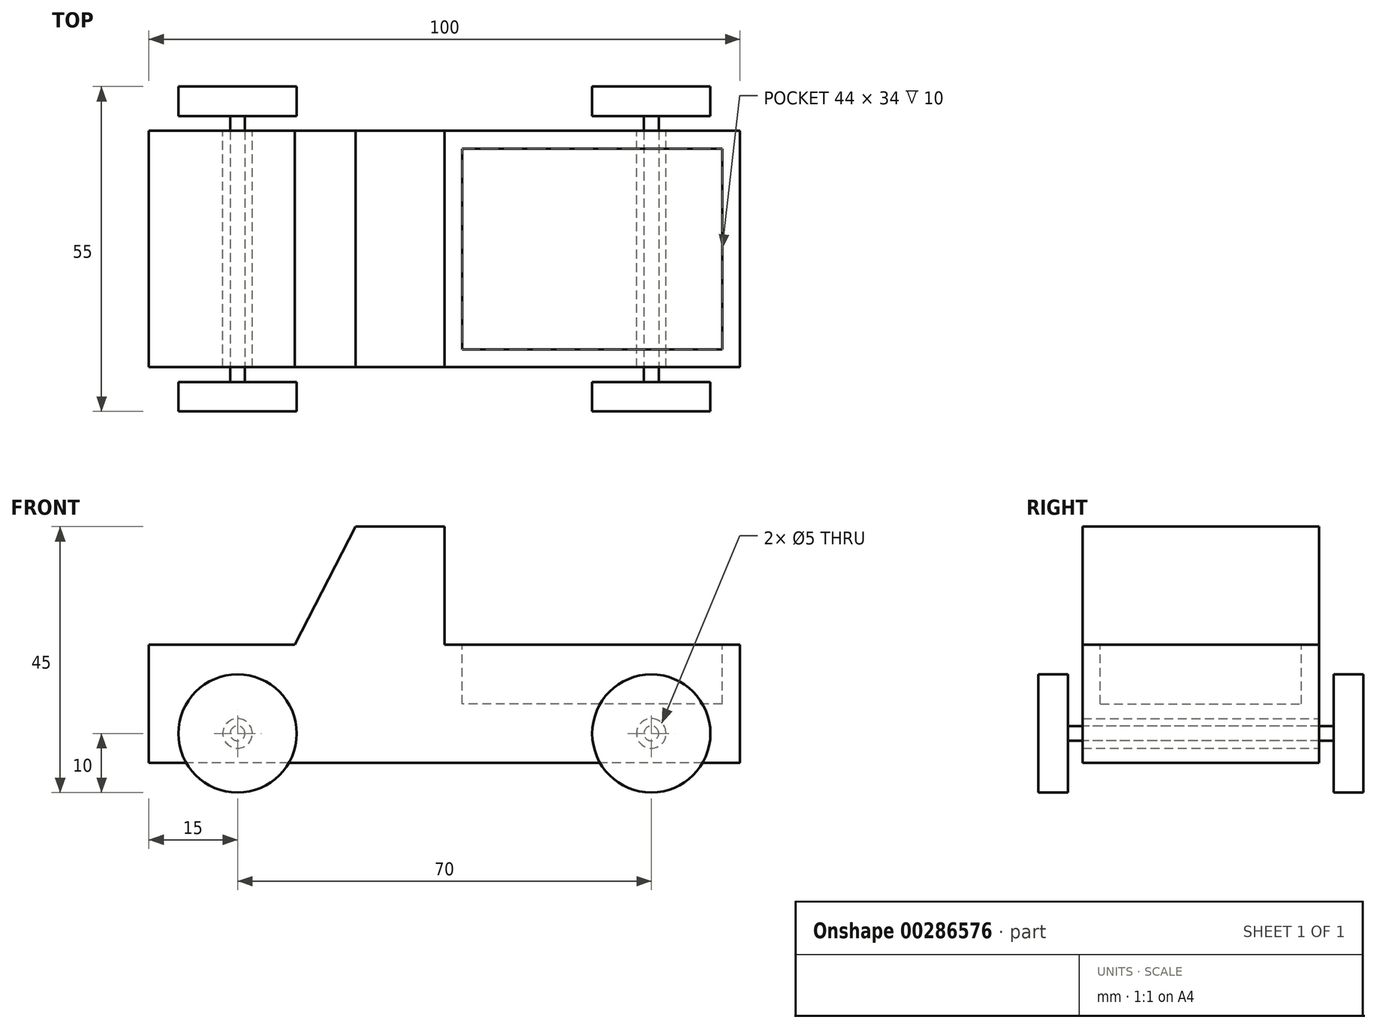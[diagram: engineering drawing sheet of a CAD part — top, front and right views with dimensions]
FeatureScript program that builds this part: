
annotation { "Feature Type Name" : "Feature", "Feature Type Description" : "" }
export const myFeature = defineFeature(function(context is Context, id is Id, definition is map)
    precondition{}
    {
        {
            var Q0;
            Q0=qCreatedBy(makeId("Front.planeOp"),FACE);
            var sketch = newSketch(context, id + "F0", { "sketchPlane" : qUnion([Q0])});
            skLineSegment(sketch, "E0.bottom", {"start": v(50, -10) * mm, "end": v(-50, -10) * mm});
            skLineSegment(sketch, "E0.left", {"start": v(50, -10) * mm, "end": v(50, 10) * mm});
            skLineSegment(sketch, "E0.right", {"start": v(-50, -10) * mm, "end": v(-50, 10) * mm});
            skPoint(sketch, "E0.middle", {"position": v(0, 0) * mm});
            skLineSegment(sketch, "E1", {"start": v(-50, 10) * mm, "end": v(-35, 10) * mm});
            skCircle(sketch, "E2", {"center": v(-35, -5) * mm, "radius": 2.5 * mm});
            skCircle(sketch, "E3", {"center": v(35, -5) * mm, "radius": 2.5 * mm});
            skLineSegment(sketch, "E4", {"start": v(50, 10) * mm, "end": v(0, 10) * mm});
            skLineSegment(sketch, "E5", {"start": v(0, 10) * mm, "end": v(0, 30) * mm});
            skLineSegment(sketch, "E6", {"start": v(0, 30) * mm, "end": v(-15, 30) * mm});
            skPoint(sketch, "E7", {"position": v(-25.3, 10) * mm});
            skLineSegment(sketch, "E8", {"start": v(-25.3, 10) * mm, "end": v(-35, 10) * mm});
            skLineSegment(sketch, "E9", {"start": v(-25.3, 10) * mm, "end": v(-15, 30) * mm});
            skSolve(sketch);
        }
        {
            var Q0;
            Q0=makeQuery(id+"F0.imprint","IMPRINT",FACE,{"disambiguationData":[TD([[makeQuery(id+"F0.imprint","IMPRINT",EDGE,{"derivedFrom":sQuery(id+"F0.wireOp",EDGE,"E0.bottom")}),-1.0]])]});
            extrude(context, id + "F1", {"entities" : qUnion([Q0]), "depth" : 40 * mm});
        }
        {
            var Q0;
            Q0=makeQuery(id+"F1.opExtrude","SWEPT_FACE",FACE,{"disambiguationData":[OSD([sQuery(id+"F0.wireOp",EDGE,"E4")])]});
            var sketch = newSketch(context, id + "F2", { "sketchPlane" : qUnion([Q0])});
            skLineSegment(sketch, "E10.0", {"start": v(47, -3) * mm, "end": v(3, -3) * mm});
            skLineSegment(sketch, "E10.1", {"start": v(47, -37) * mm, "end": v(47, -3) * mm});
            skLineSegment(sketch, "E10.2", {"start": v(3, -37) * mm, "end": v(47, -37) * mm});
            skLineSegment(sketch, "E10.3", {"start": v(3, -3) * mm, "end": v(3, -37) * mm});
            skSolve(sketch);
        }
        {
            var Q0;
            Q0=makeQuery(id+"F2.imprint","IMPRINT",FACE,{"disambiguationData":[TD([[makeQuery(id+"F2.imprint","IMPRINT",EDGE,{"derivedFrom":sQuery(id+"F2.wireOp",EDGE,"E10.0")}),1.0]])]});
            extrude(context, id + "F3", {"entities" : qUnion([Q0]), "operationType" : NewBodyOperationType.REMOVE, "oppositeDirection" : true, "depth" : 10 * mm});
        }
        {
            var Q0;
            Q0=makeQuery(id+"F1.opExtrude","CAP_FACE",FACE,{"disambiguationData":[OSD([sQuery(id+"F0.wireOp",EDGE,"E0.bottom"),sQuery(id+"F0.wireOp",EDGE,"E0.left"),sQuery(id+"F0.wireOp",EDGE,"E0.right"),sQuery(id+"F0.wireOp",EDGE,"E1"),sQuery(id+"F0.wireOp",EDGE,"E2"),sQuery(id+"F0.wireOp",EDGE,"E3"),sQuery(id+"F0.wireOp",EDGE,"E4"),sQuery(id+"F0.wireOp",EDGE,"E5"),sQuery(id+"F0.wireOp",EDGE,"E6"),sQuery(id+"F0.wireOp",EDGE,"E8"),sQuery(id+"F0.wireOp",EDGE,"E9")])],"isStart":false});
            var sketch = newSketch(context, id + "F4", { "sketchPlane" : qUnion([Q0])});
            skPoint(sketch, "E11", {"position": v(35, -5) * mm});
            skCircle(sketch, "E12", {"center": v(35, -5) * mm, "radius": 1.25 * mm});
            skSolve(sketch);
        }
        {
            var Q0;
            Q0=makeQuery(id+"F4.imprint","IMPRINT",FACE,{"disambiguationData":[TD([[makeQuery(id+"F4.imprint","IMPRINT",EDGE,{"derivedFrom":sQuery(id+"F4.wireOp",EDGE,"E12")}),1.0]])]});
            extrude(context, id + "F5", {"entities" : qUnion([Q0]), "operationType" : NewBodyOperationType.ADD, "oppositeDirection" : true, "depth" : 42.5 * mm});
        }
        {
            var Q0;
            Q0=makeQuery(id+"F5.opExtrude","CAP_FACE",FACE,{"disambiguationData":[OSD([sQuery(id+"F4.wireOp",EDGE,"E12")])],"isStart":true});
            extrude(context, id + "F6", {"entities" : qUnion([Q0]), "operationType" : NewBodyOperationType.ADD, "depth" : 2.5 * mm});
        }
        {
            var Q0;
            Q0=makeQuery(id+"F1.opExtrude","CAP_FACE",FACE,{"disambiguationData":[OSD([sQuery(id+"F0.wireOp",EDGE,"E0.bottom"),sQuery(id+"F0.wireOp",EDGE,"E0.left"),sQuery(id+"F0.wireOp",EDGE,"E0.right"),sQuery(id+"F0.wireOp",EDGE,"E1"),sQuery(id+"F0.wireOp",EDGE,"E2"),sQuery(id+"F0.wireOp",EDGE,"E3"),sQuery(id+"F0.wireOp",EDGE,"E4"),sQuery(id+"F0.wireOp",EDGE,"E5"),sQuery(id+"F0.wireOp",EDGE,"E6"),sQuery(id+"F0.wireOp",EDGE,"E8"),sQuery(id+"F0.wireOp",EDGE,"E9")])],"isStart":false});
            var sketch = newSketch(context, id + "F7", { "sketchPlane" : qUnion([Q0])});
            skCircle(sketch, "E13", {"center": v(-35, -5) * mm, "radius": 1.25 * mm});
            skSolve(sketch);
        }
        {
            var Q0;
            Q0=makeQuery(id+"F7.imprint","IMPRINT",FACE,{"disambiguationData":[TD([[makeQuery(id+"F7.imprint","IMPRINT",EDGE,{"derivedFrom":sQuery(id+"F7.wireOp",EDGE,"E13")}),1.0]])]});
            extrude(context, id + "F8", {"entities" : qUnion([Q0]), "operationType" : NewBodyOperationType.ADD, "oppositeDirection" : true, "depth" : 42.5 * mm});
        }
        {
            var Q0;
            Q0=makeQuery(id+"F8.opExtrude","CAP_FACE",FACE,{"disambiguationData":[OSD([sQuery(id+"F7.wireOp",EDGE,"E13")])],"isStart":true});
            extrude(context, id + "F9", {"entities" : qUnion([Q0]), "operationType" : NewBodyOperationType.ADD, "depth" : 2.5 * mm});
        }
        {
            var Q0;
            Q0=makeQuery(id+"F6.opExtrude","CAP_FACE",FACE,{"disambiguationData":[OSD([sQuery(id+"F4.wireOp",EDGE,"E12")])],"isStart":false});
            var sketch = newSketch(context, id + "F10", { "sketchPlane" : qUnion([Q0])});
            skCircle(sketch, "E14", {"center": v(35, -5) * mm, "radius": 10 * mm});
            skSolve(sketch);
        }
        {
            var Q0;
            Q0=makeQuery(id+"F9.opExtrude","CAP_FACE",FACE,{"disambiguationData":[OSD([sQuery(id+"F7.wireOp",EDGE,"E13")])],"isStart":false});
            var sketch = newSketch(context, id + "F11", { "sketchPlane" : qUnion([Q0])});
            skCircle(sketch, "E15", {"center": v(-35, -5) * mm, "radius": 10 * mm});
            skSolve(sketch);
        }
        {
            var Q0;
            Q0=makeQuery(id+"F11.imprint","IMPRINT",FACE,{"disambiguationData":[TD([[makeQuery(id+"F11.imprint","IMPRINT",EDGE,{"derivedFrom":sQuery(id+"F11.wireOp",EDGE,"E15")}),1.0]])]});
            var Q1;
            Q1=makeQuery(id+"F10.imprint","IMPRINT",FACE,{"disambiguationData":[TD([[makeQuery(id+"F10.imprint","IMPRINT",EDGE,{"derivedFrom":sQuery(id+"F10.wireOp",EDGE,"E14")}),1.0]])]});
            extrude(context, id + "F12", {"entities" : qUnion([Q0, Q1]), "operationType" : NewBodyOperationType.ADD, "depth" : 5 * mm});
        }
        {
            var Q0;
            Q0=makeQuery(id+"F5.opExtrude","CAP_FACE",FACE,{"disambiguationData":[OSD([sQuery(id+"F4.wireOp",EDGE,"E12")])],"isStart":false});
            var sketch = newSketch(context, id + "F13", { "sketchPlane" : qUnion([Q0])});
            skCircle(sketch, "E16", {"center": v(-35, -5) * mm, "radius": 10 * mm});
            skSolve(sketch);
        }
        {
            var Q0;
            Q0=makeQuery(id+"F8.opExtrude","CAP_FACE",FACE,{"disambiguationData":[OSD([sQuery(id+"F7.wireOp",EDGE,"E13")])],"isStart":false});
            var sketch = newSketch(context, id + "F14", { "sketchPlane" : qUnion([Q0])});
            skCircle(sketch, "E17", {"center": v(35, -5) * mm, "radius": 10 * mm});
            skSolve(sketch);
        }
        {
            var Q0;
            Q0=makeQuery(id+"F13.imprint","IMPRINT",FACE,{"disambiguationData":[TD([[makeQuery(id+"F13.imprint","IMPRINT",EDGE,{"derivedFrom":sQuery(id+"F13.wireOp",EDGE,"E16")}),1.0]])]});
            var Q1;
            Q1=makeQuery(id+"F14.imprint","IMPRINT",FACE,{"disambiguationData":[TD([[makeQuery(id+"F14.imprint","IMPRINT",EDGE,{"derivedFrom":sQuery(id+"F14.wireOp",EDGE,"E17")}),1.0]])]});
            var Q2;
            Q2=makeQuery(id+"F13.imprint","IMPRINT",FACE,{"disambiguationData":[TD([[makeQuery(id+"F13.imprint","IMPRINT",EDGE,{"derivedFrom":makeQuery(id+"F5.opExtrude","CAP_EDGE",EDGE,{"disambiguationData":[OSD([sQuery(id+"F4.wireOp",EDGE,"E12")])],"isStart":false})}),-1.0]])]});
            var Q3;
            Q3=makeQuery(id+"F14.imprint","IMPRINT",FACE,{"disambiguationData":[TD([[makeQuery(id+"F14.imprint","IMPRINT",EDGE,{"derivedFrom":makeQuery(id+"F8.opExtrude","CAP_EDGE",EDGE,{"disambiguationData":[OSD([sQuery(id+"F7.wireOp",EDGE,"E13")])],"isStart":false})}),-1.0]])]});
            extrude(context, id + "F15", {"entities" : qUnion([Q0, Q1, Q2, Q3]), "operationType" : NewBodyOperationType.ADD, "depth" : 5 * mm});
        }
        {
            var Q0;
            Q0=makeQuery(id+"F12.opExtrude","SWEPT_BODY",BODY,{"disambiguationData":[OSD([sQuery(id+"F7.wireOp",EDGE,"E13"),sQuery(id+"F11.wireOp",EDGE,"E15")])]});
            deleteBodies(context, id + "F16", {"entities" : qUnion([Q0])});
        }
        {
            var Q0;
            Q0=makeQuery(id+"F12.opExtrude","SWEPT_BODY",BODY,{"disambiguationData":[OSD([sQuery(id+"F4.wireOp",EDGE,"E12"),sQuery(id+"F10.wireOp",EDGE,"E14")])]});
            deleteBodies(context, id + "F17", {"entities" : qUnion([Q0])});
        }
        {
            var Q0;
            Q0 = qSketchRegion(id + "F11", true);
            var Q1;
            Q1 = qSketchRegion(id + "F10", true);
            var Q2;
            Q2=makeQuery(id+"F9.opExtrude","CAP_FACE",FACE,{"disambiguationData":[OSD([sQuery(id+"F7.wireOp",EDGE,"E13")])],"isStart":false});
            var Q3;
            Q3=makeQuery(id+"F6.opExtrude","CAP_FACE",FACE,{"disambiguationData":[OSD([sQuery(id+"F4.wireOp",EDGE,"E12")])],"isStart":false});
            extrude(context, id + "F18", {"entities" : qUnion([Q0, Q1, Q2, Q3]), "operationType" : NewBodyOperationType.ADD, "depth" : 5 * mm});
        }
    });
